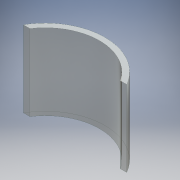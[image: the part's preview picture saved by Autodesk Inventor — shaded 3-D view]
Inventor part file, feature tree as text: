
AUTODESK INVENTOR PART (.ipt)
format: ipt  version: 2016 (Build 200138000, 138)  size: 99,840 bytes
history: native  units: mm
features: other x1, extrude x1, sketch x1
ambient origin geometry x8: Origin, YZ Plane, XZ Plane, XY Plane, X Axis, Y Axis, Z Axis, Center Point
bodies: Body1 (feature_tree)
feature tree (3):
  other  "ソリッド1"
  extrude  "押し出し1"  TaperAngle=30.0deg  [1 undecoded]
  sketch  "スケッチ1"
note: 1 required parameter value undecoded (feature->parameter linkage not recoverable at this tier; creation-order binding heuristic only, values carry confidence <= 0.55)
